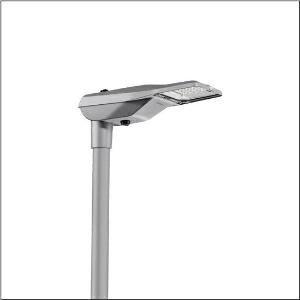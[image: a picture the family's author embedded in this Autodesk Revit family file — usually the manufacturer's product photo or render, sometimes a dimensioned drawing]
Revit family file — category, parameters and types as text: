
# Revit family: streetlight_sl_21_micro___pl52_5xe1h33t08db_704d
name_source: partatom
category: Lighting Fixtures
units: mm (PartAtom-declared; Revit-internal decimal feet)

## family parameters
Cut with Voids When Loaded = No
Host = Face
Light Source = No
Part Type = Normal
Room Calculation Point = No
Round Connector Dimension = Use Diameter
Shared = No

## types (1)
- --- (1 x LED, 5020 lm, 39.1 W, 3000K)
    Apparent Load = 39 VA
    CIE Flux Codes = 27 59 98 100 100
    Color Rendering = 70
    Color Temperature = 3000K
    Default Elevation = 1800 mm
    Description = Streetlight SL 21 micro, mast luminaire, primary light control with lens, of PMMA, primary optical cover: cover, of toughened safety glass, transparent, light distribution: PL52, light emission: direct distribution, primary light characteristic: asymmetric, installation type: side-entry, post-top, LED, High Power LED, rated luminous flux: 5.020lm, luminous efficacy: 128lm/W, light colour: 730, colour temperature: 3000K, control: flexible luminous flux parameterisation, time-dependent luminous flux control, constant luminous flux control, overheat protection, presetting dimming logarithmic, mains connection: 220..240V, AC, 50/60Hz, start of lifetime: 39W, end of service life: 41W, reduction: 18W, luminaire housing, of diecast aluminium, powder-coated, Siteco® metallic grey (DB 702S), corrosivity category C5 mid according to DIN EN ISO 12944, please order mast flange separately, inclination adjustable: 0°, 5°, 10°, 15°, sealing non-destructively replaceable, multi-level sealing system, length: 528mm, width: 235mm, height: 110mm, mast flange for spigot size: 42mm (side-entry): 5XC10008XM4, 60/48mm (side-entry/post-top): 5XC10108XM2, 76/60mm (side-entry/post-top): 5XC10108XM1, Smart Interface below and above, protection rating (complete): IP66, insulation class (complete): insulation class II (safety insulation), certification: CE, ENEC, ENEC+, VDE, impact resistance: IK09, permissible operating ambient temperature for outdoor applications: -40..+50°C, standard-compliant lighting for roads and squares, packaging unit: 1 piece

Light Distribution: PL52
    Height = 110 mm
    Lamp = 1 x LED
    Lamp Light Flux = 5020 lm
    Lamp Power = 39.1 W
    Lamp count = 1
    Length = 528 mm
    Luminous efficacy = 128 lm/W
    Manufacturer = Siteco
    ModVariant = No
    Model = 5XE1H33T08DB
    Number of Poles = 1
    OnlyDefault = Yes
    Power Factor = 1
    Product Name = Streetlight SL 21 micro | PL52
    Product group = mast luminaire | pylon top
    ProductGroupID = 6100
    Protection Class = Protection class II
    Protection Degree = IP 66
    RLX_Detail_Level = 1
    RLX_Emergency_Light_Flux = 0 lm
    RLX_Emergency_Type = 0
    RLX_Emergency_Type_DB = No
    RlxData = <blob elided: 107913 chars, md5=1dfab503>
    Socket = socket
    Standby Power = 0 W
    System Light Flux = 5020 lm
    System Power = 39 W
    Type Comments = factory setting: luminous flux: 100 % | dim-lin: 254 | 765 mA
    Type Image = l_1007239.jpg
    URL = http://relux.com
    VarID = @adj_106329
    Voltage = 0 V
    Weight = 0.00 kg
    Width = 235 mm

## geometry (parser evidence)
native form markers: Blend x4, Sweep x10
no freeform markers — native parametric forms only
